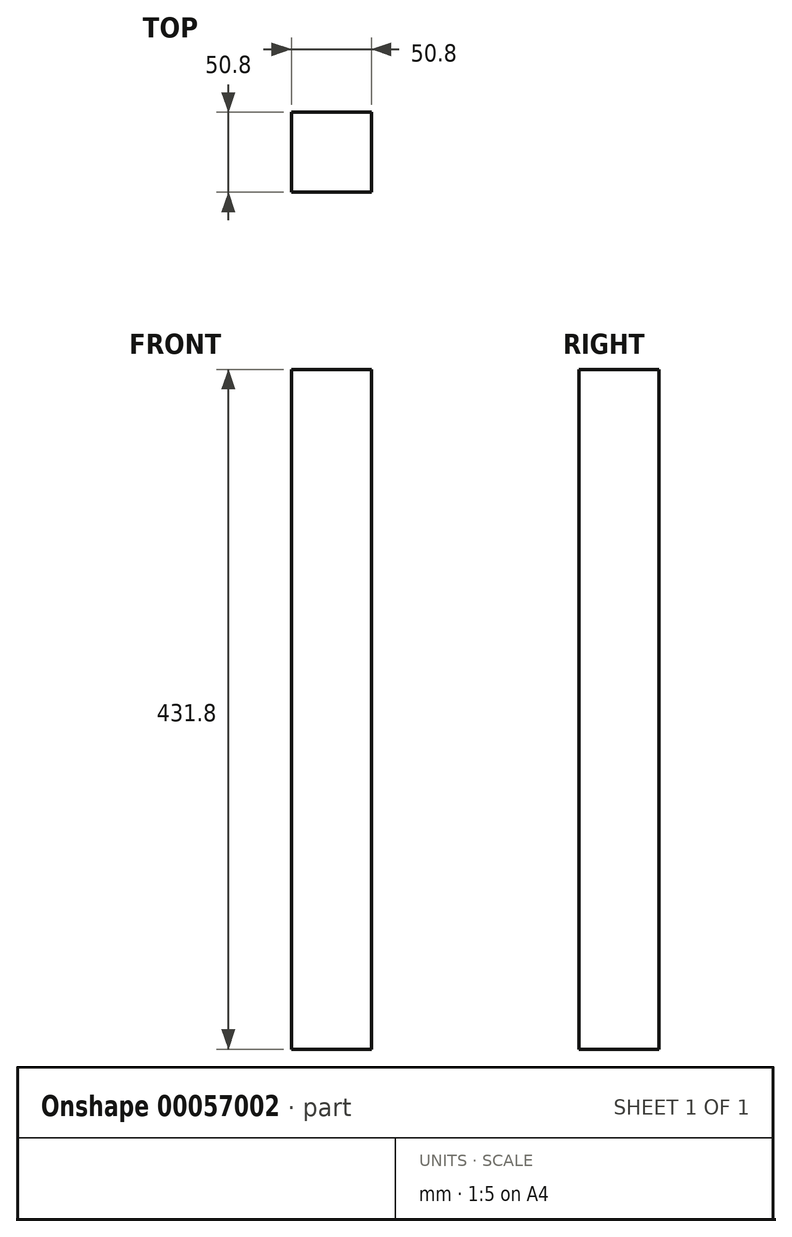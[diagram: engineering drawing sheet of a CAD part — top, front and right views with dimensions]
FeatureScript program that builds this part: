
annotation { "Feature Type Name" : "Feature", "Feature Type Description" : "" }
export const myFeature = defineFeature(function(context is Context, id is Id, definition is map)
    precondition{}
    {
        {
            var Q0;
            Q0=qCreatedBy(makeId("Top.planeOp"),FACE);
            var sketch = newSketch(context, id + "F0", { "sketchPlane" : qUnion([Q0])});
            skLineSegment(sketch, "E0.bottom", {"start": v(25.4, -25.4) * mm, "end": v(-25.4, -25.4) * mm});
            skLineSegment(sketch, "E0.top", {"start": v(25.4, 25.4) * mm, "end": v(-25.4, 25.4) * mm});
            skLineSegment(sketch, "E0.left", {"start": v(25.4, -25.4) * mm, "end": v(25.4, 25.4) * mm});
            skLineSegment(sketch, "E0.right", {"start": v(-25.4, -25.4) * mm, "end": v(-25.4, 25.4) * mm});
            skLineSegment(sketch, "E1", {"start": v(-25.4, 25.4) * mm, "end": v(25.4, -25.4) * mm, "construction": true});
            skSolve(sketch);
        }
        {
            var Q0;
            Q0=makeQuery(id+"F0.imprint","IMPRINT",FACE,{"disambiguationData":[TD([[makeQuery(id+"F0.imprint","IMPRINT",EDGE,{"derivedFrom":sQuery(id+"F0.wireOp",EDGE,"E0.bottom")}),-1.0]])]});
            extrude(context, id + "F1", {"entities" : qUnion([Q0]), "depth" : 431.8 * mm});
        }
    });
